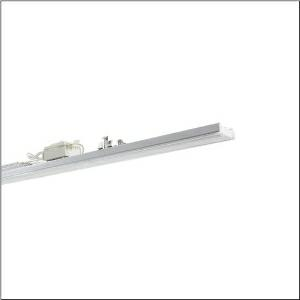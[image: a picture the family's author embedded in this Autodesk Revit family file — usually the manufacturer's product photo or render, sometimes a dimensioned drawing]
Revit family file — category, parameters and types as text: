
# Revit family: licross_r__21_recessed_mo_52te12dv4fxgd_6a3b
name_source: partatom
category: Lighting Fixtures
units: mm (PartAtom-declared; Revit-internal decimal feet)

## family parameters
Cut with Voids When Loaded = No
Host = Face
Light Source = No
Part Type = Normal
Room Calculation Point = No
Round Connector Dimension = Use Diameter
Shared = No

## types (1)
- --- (1 x LED, 15420 lm, 85.3 W, 4000K)
    Apparent Load = 85 VA
    CIE Flux Codes = 72 92 99 100 100
    Color Rendering = 80
    Color Temperature = 4000K
    Default Elevation = 1800 mm
    Description = Licross® 21 Recessed MO, luminaire insert, of sheet steel, galvanised, coil coated, white, length: 2.250mm, width: 66mm, height: 67mm, LED rated luminous flux: 15.420lm, light colour: 840, control gear: DALI 2 (for two DALI lines), with plug, 6-pole, with phase selection, mains connection: 220..240V, AC/DC, 0/50..60Hz, rated input power: 85W, without changeover relay, for emergency light function, for central battery installations according to DIN EN 60598-2-22, internal wiring halogen-free, primary optical cover: cover, of PMMA, light emission: direct distribution, primary light characteristic: symmetric, protection rating (complete): IP54, insulation class (complete): insulation class I (protective earthing), certification: CE, ENEC, VDE, UKCA, protection symbol: D if used in an environment with non-conductive dust loads with corresponding accessories, impact resistance: IK06, permissible ambient temperature for indoor applications: -25..+35°C, standard: EN 60598-2-22, corresponds to IFS (International Featured Standards) requirements for safety and quality in the food industry, reducing of maximum allowable ambient temperature of 5°C with ceiling mounting, LABS conformity tested according to VDMA 24364:2018-05, packaging unit: 1 piece
    Height = 58 mm
    Lamp = 1 x LED
    Lamp Light Flux = 15420 lm
    Lamp Power = 85.3 W
    Lamp count = 1
    Length = 2250 mm
    Luminous efficacy = 181 lm/W
    Manufacturer = Siteco
    ModVariant = No
    Model = 52TE12DV4FXGD
    Mounting Place = Ceiling
    Mounting Type = Pendant
    Number of Poles = 1
    OnlyDefault = Yes
    Power Factor = 1
    Product Name = Licross® 21 Recessed MO
    Product group = luminaire insert | ceiling pendant
    ProductGroupID = 902
    Protection Class = Protection class I
    Protection Degree = IP 54
    RLX_Detail_Level = 1
    RLX_Emergency_Light_Flux = 0 lm
    RLX_Emergency_Type = 0
    RLX_Emergency_Type_DB = No
    RlxData = <blob elided: 30037 chars, md5=0c72ff9d>
    Socket = socket
    Standby Power = 0 W
    System Light Flux = 15420 lm
    System Power = 85 W
    Type Comments = : AC-mode, luminous flux: 100 % | dim-lin: 254 | 390 mA
    Type Image = l_1296930.jpg
    URL = http://relux.com
    VarID = @adj_134495
    Voltage = 0 V
    Weight = 0.00 kg
    Width = 66 mm

## geometry (parser evidence)
native form markers: Blend x4, Sweep x8
no freeform markers — native parametric forms only
